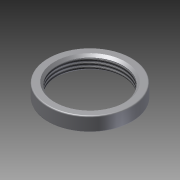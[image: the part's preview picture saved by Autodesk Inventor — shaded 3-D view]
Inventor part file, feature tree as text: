
AUTODESK INVENTOR PART (.ipt)
format: ipt  version: 2014 (Build 180170000, 170)  size: 101,888 bytes
history: native  units: mm (DEFAULTED — no unit token found)
features: extrude x1, thread x1, chamfer x1, fillet x1, sketch x1
ambient origin geometry x8: Origin, YZ Plane, XZ Plane, XY Plane, X Axis, Y Axis, Z Axis, Center Point
bodies: Solid1 (feature_tree)
feature tree (5):
  extrude  "Extrusion1"  Depth=0.5mm
  thread  "Thread1"  [1 undecoded]
  chamfer  "Chamfer1"  Distance=0.5mm
  fillet  "Fillet1"  [1 undecoded]
  sketch  "Sketch1"  dims[d0=37.0mm d1=29.0mm d2=6.2mm d3=0.0mm d4=10.0mm d5=0.0mm d6=1.0mm d7=2.0mm d8=45.0deg d9=0.5mm]
note: 2 required parameter values undecoded (feature->parameter linkage not recoverable at this tier; creation-order binding heuristic only, values carry confidence <= 0.55)
